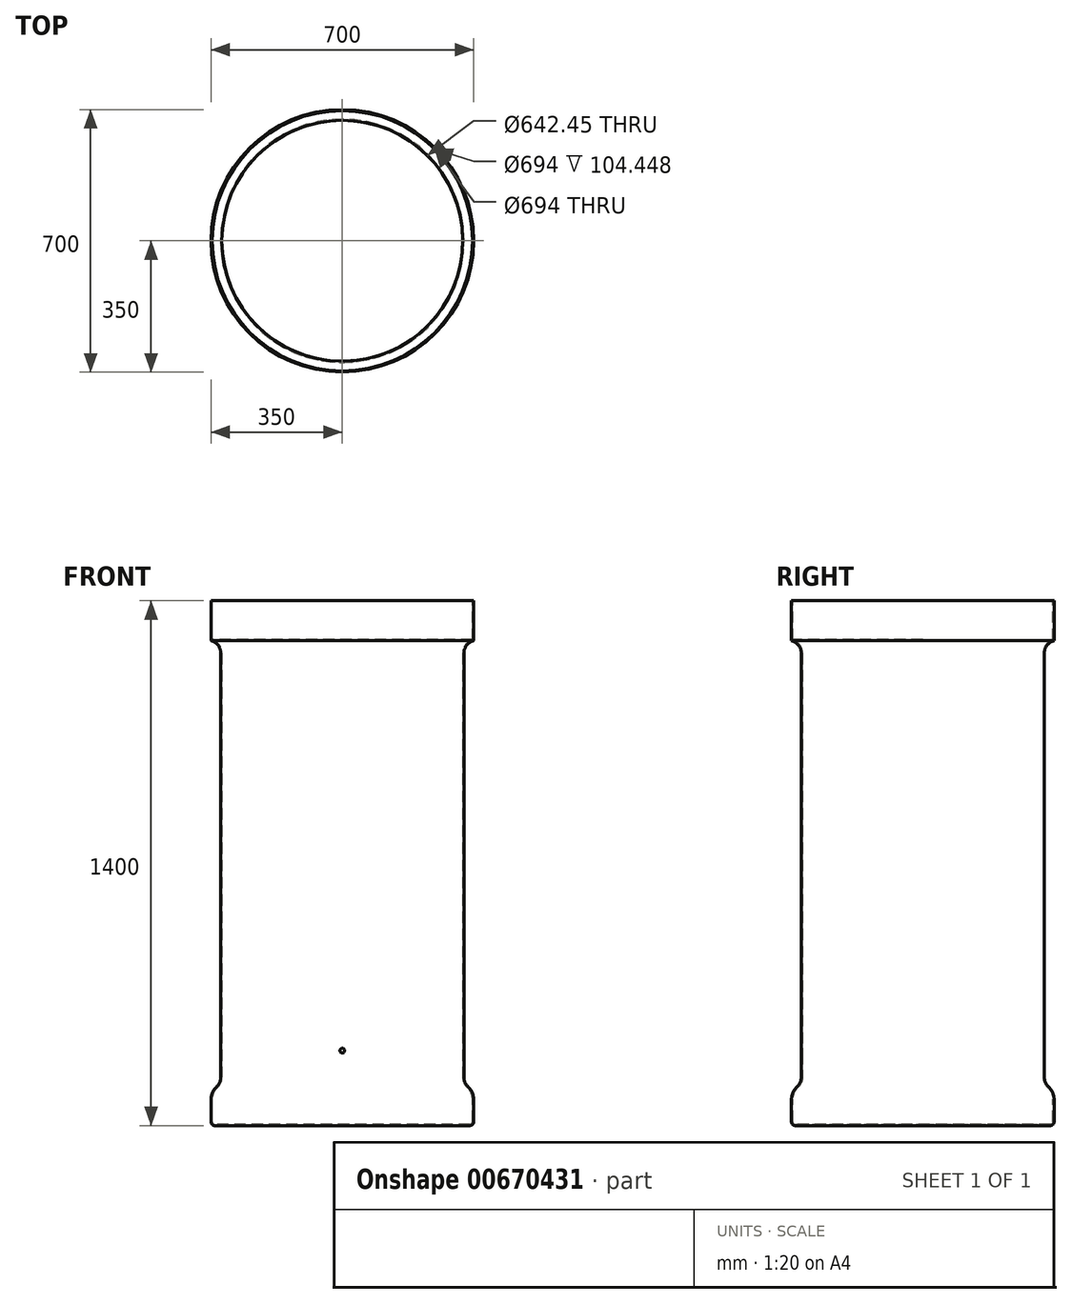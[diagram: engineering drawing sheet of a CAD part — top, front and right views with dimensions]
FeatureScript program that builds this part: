
annotation { "Feature Type Name" : "Feature", "Feature Type Description" : "" }
export const myFeature = defineFeature(function(context is Context, id is Id, definition is map)
    precondition{}
    {
        {
            var Q0;
            Q0=qCreatedBy(makeId("Top.planeOp"),FACE);
            var sketch = newSketch(context, id + "F0", { "sketchPlane" : qUnion([Q0])});
            skCircle(sketch, "E0", {"center": v(0, 0) * mm, "radius": 350 * mm});
            skSolve(sketch);
        }
        {
            var Q0;
            Q0=makeQuery(id+"F0.imprint","IMPRINT",FACE,{"disambiguationData":[TD([[makeQuery(id+"F0.imprint","IMPRINT",EDGE,{"derivedFrom":sQuery(id+"F0.wireOp",EDGE,"E0")}),1.0]])]});
            extrude(context, id + "F1", {"entities" : qUnion([Q0]), "oppositeDirection" : true, "depth" : 1400 * mm, "offsetDistance" : 25 * mm});
        }
        {
            var Q0;
            Q0=qCreatedBy(makeId("Front.planeOp"),FACE);
            var sketch = newSketch(context, id + "F2", { "sketchPlane" : qUnion([Q0])});
            skLineSegment(sketch, "E1.0.0", {"start": v(350, -1400) * mm, "end": v(-350, -1400) * mm, "construction": true});
            skLineSegment(sketch, "E2", {"start": v(0, -1400) * mm, "end": v(0, -1200) * mm, "construction": true});
            skCircle(sketch, "E3", {"center": v(0, -1200) * mm, "radius": 6.35 * mm});
            skSolve(sketch);
        }
        {
            var Q0;
            Q0=qCreatedBy(makeId("Front.planeOp"),FACE);
            var sketch = newSketch(context, id + "F3", { "sketchPlane" : qUnion([Q0])});
            skLineSegment(sketch, "E4", {"start": v(350, 0) * mm, "end": v(350, -1400) * mm, "construction": true});
            skLineSegment(sketch, "E5", {"start": v(-350, -1400) * mm, "end": v(-350, 0) * mm, "construction": true});
            skLineSegment(sketch, "E6.bottom", {"start": v(350, -106.74) * mm, "end": v(324.22, -106.74) * mm});
            skLineSegment(sketch, "E6.top", {"start": v(350, -1288.69) * mm, "end": v(324.22, -1288.69) * mm});
            skLineSegment(sketch, "E6.left", {"start": v(350, -106.74) * mm, "end": v(350, -1288.69) * mm});
            skLineSegment(sketch, "E6.right", {"start": v(324.22, -106.74) * mm, "end": v(324.22, -1288.69) * mm});
            skLineSegment(sketch, "E7", {"start": v(-350, 0) * mm, "end": v(350, 0) * mm, "construction": true});
            skLineSegment(sketch, "E8", {"start": v(0, 0) * mm, "end": v(0, -1400) * mm, "construction": true});
            skSolve(sketch);
        }
        {
            var Q0;
            Q0=makeQuery(id+"F3.imprint","IMPRINT",FACE,{"disambiguationData":[TD([[makeQuery(id+"F3.imprint","IMPRINT",EDGE,{"derivedFrom":sQuery(id+"F3.wireOp",EDGE,"E6.bottom")}),1.0]])]});
            var Q1;
            Q1=sQuery(id+"F3.wireOp",EDGE,"E8");
            revolve(context, id + "F4", {"operationType" : NewBodyOperationType.REMOVE, "entities" : qUnion([Q0]), "axis" : qUnion([Q1]), "revolveType" : RevolveType.FULL, "oppositeDirection" : true});
        }
        {
            var Q0;
            Q0=makeQuery(id+"F4.boolean.opBoolean","COPY",EDGE,{"derivedFrom":makeQuery(id+"F4.opRevolve","SWEPT_EDGE",EDGE,{"disambiguationData":[OSD([sQuery(id+"F3.wireOp",EDGE,"E6.bottom"),sQuery(id+"F3.wireOp",EDGE,"E6.left")])]})});
            var Q1;
            Q1=makeQuery(id+"F4.boolean.opBoolean","COPY",EDGE,{"derivedFrom":makeQuery(id+"F4.opRevolve","SWEPT_EDGE",EDGE,{"disambiguationData":[OSD([sQuery(id+"F3.wireOp",EDGE,"E6.top"),sQuery(id+"F3.wireOp",EDGE,"E6.left")])]})});
            fillet(context, id + "F5", {"entities" : qUnion([Q0, Q1]), "radius" : 45.87 * mm, "tangentPropagation" : true, "allowEdgeOverflow" : false});
        }
        {
            var Q0;
            Q0=makeQuery(id+"F4.boolean.opBoolean","COPY",FACE,{"derivedFrom":makeQuery(id+"F4.opRevolve","SWEPT_FACE",FACE,{"disambiguationData":[OSD([sQuery(id+"F3.wireOp",EDGE,"E6.right")])]})});
            fillet(context, id + "F6", {"entities" : qUnion([Q0]), "radius" : 33.46 * mm, "tangentPropagation" : true, "allowEdgeOverflow" : false});
        }
        {
            var Q0;
            Q0=makeQuery(id+"F1.opExtrude","CAP_EDGE",EDGE,{"disambiguationData":[OSD([sQuery(id+"F0.wireOp",EDGE,"E0")])],"isStart":false});
            fillet(context, id + "F7", {"entities" : qUnion([Q0]), "radius" : 9.66 * mm, "tangentPropagation" : true, "allowEdgeOverflow" : false});
        }
        {
            var Q0;
            Q0=makeQuery(id+"F1.opExtrude","CAP_FACE",FACE,{"disambiguationData":[OSD([sQuery(id+"F0.wireOp",EDGE,"E0")])],"isStart":true});
            shell(context, id + "F8", {"entities" : qUnion([Q0]), "thickness" : 3 * mm});
        }
        {
            var Q0;
            Q0 = qSketchRegion(id + "F2", true);
            var Q1;
            Q1=makeQuery(id+"F4.boolean.opBoolean","COPY",FACE,{"derivedFrom":makeQuery(id+"F4.opRevolve","SWEPT_FACE",FACE,{"disambiguationData":[OSD([sQuery(id+"F3.wireOp",EDGE,"E6.right")])]})});
            extrude(context, id + "F9", {"entities" : qUnion([Q0]), "operationType" : NewBodyOperationType.REMOVE, "endBound" : BoundingType.UP_TO_SURFACE, "depth" : 861 * mm, "endBoundEntityFace" : qUnion([Q1]), "offsetDistance" : 25 * mm});
        }
        {
            var Q0;
            Q0=qCreatedBy(makeId("Right.planeOp"),FACE);
            var sketch = newSketch(context, id + "F10", { "sketchPlane" : qUnion([Q0])});
            skLineSegment(sketch, "E9", {"start": v(-324.22, -1193.65) * mm, "end": v(-321.22, -1193.65) * mm, "construction": true});
            skLineSegment(sketch, "E10", {"start": v(-321.22, -1206.35) * mm, "end": v(-324.22, -1206.35) * mm, "construction": true});
            skLineSegment(sketch, "E11", {"start": v(-322.72, -1193.65) * mm, "end": v(-322.72, -1206.35) * mm, "construction": true});
            skLineSegment(sketch, "E12", {"start": v(-322.72, -1200) * mm, "end": v(-316.08, -1200) * mm, "construction": true});
            skSolve(sketch);
        }
    });
